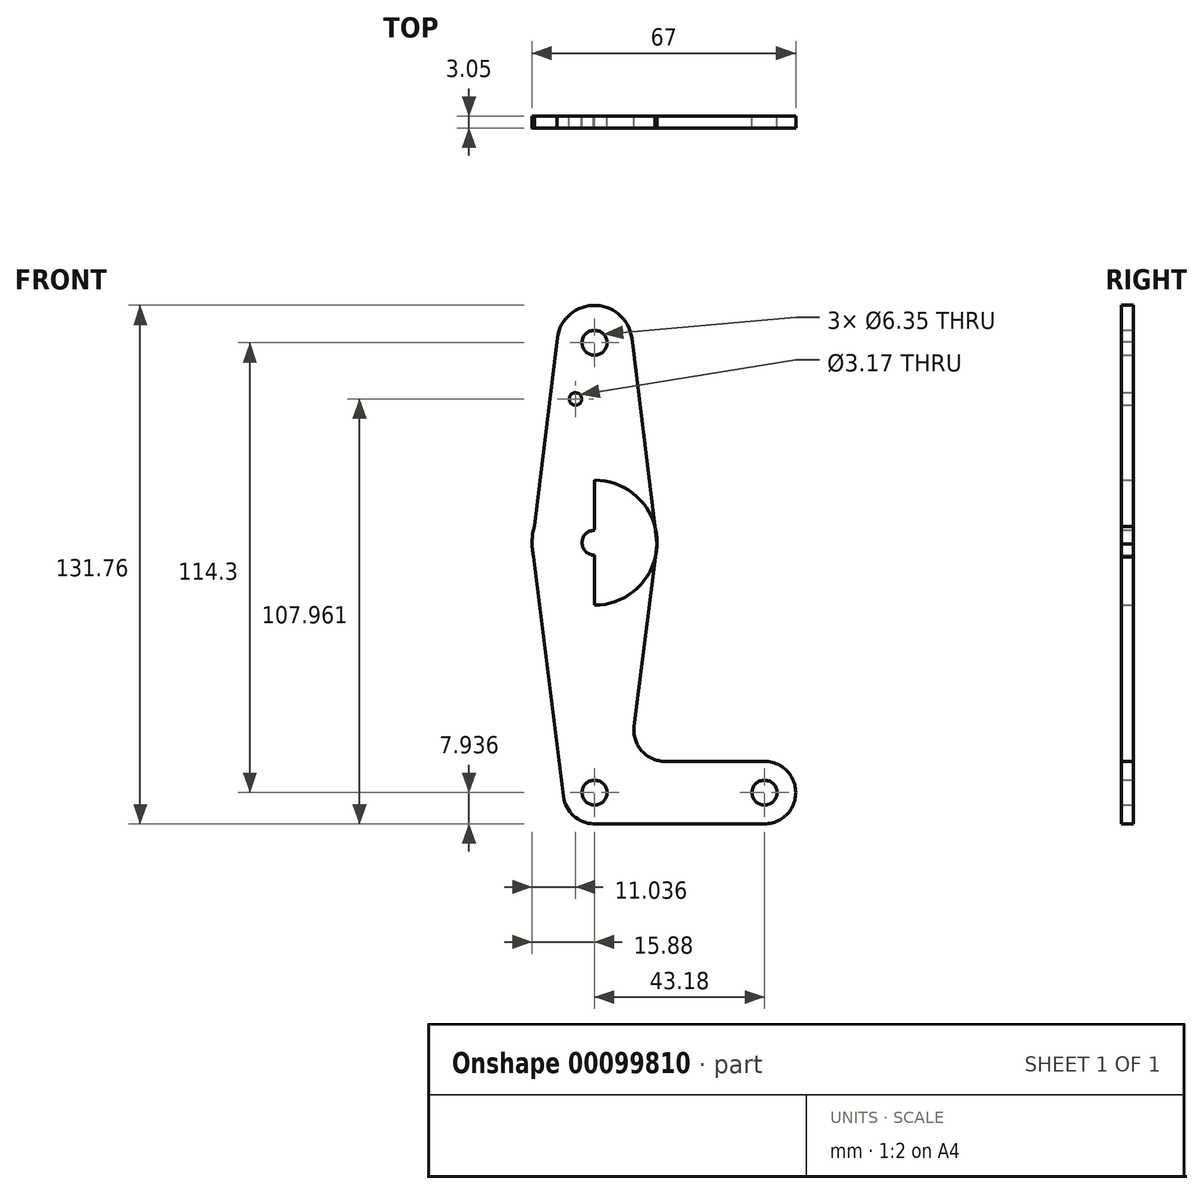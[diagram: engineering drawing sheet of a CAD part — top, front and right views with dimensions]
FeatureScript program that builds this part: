
annotation { "Feature Type Name" : "Feature", "Feature Type Description" : "" }
export const myFeature = defineFeature(function(context is Context, id is Id, definition is map)
    precondition{}
    {
        {
            var Q0;
            Q0=qCreatedBy(makeId("Front.planeOp"),FACE);
            var sketch = newSketch(context, id + "F0", { "sketchPlane" : qUnion([Q0])});
            skLineSegment(sketch, "E0", {"start": v(15.25, 82.35) * mm, "end": v(15.25, -31.95) * mm});
            skLineSegment(sketch, "E1", {"start": v(15.25, -31.95) * mm, "end": v(58.43, -31.95) * mm});
            skCircle(sketch, "E2", {"center": v(15.25, 82.35) * mm, "radius": 9.53 * mm});
            skCircle(sketch, "E3", {"center": v(15.25, 31.55) * mm, "radius": 15.88 * mm});
            skCircle(sketch, "E4", {"center": v(15.25, -31.95) * mm, "radius": 7.94 * mm});
            skCircle(sketch, "E5", {"center": v(58.43, -31.95) * mm, "radius": 7.94 * mm});
            skLineSegment(sketch, "E6", {"start": v(5.73, 82.64) * mm, "end": v(-0.62, 31.15) * mm});
            skLineSegment(sketch, "E7", {"start": v(-0.62, 31.15) * mm, "end": v(7.37, -32.94) * mm});
            skLineSegment(sketch, "E8", {"start": v(24.7, 83.5) * mm, "end": v(31.12, 31.25) * mm});
            skLineSegment(sketch, "E9", {"start": v(31.12, 31.25) * mm, "end": v(25.3, -15.08) * mm});
            skLineSegment(sketch, "E10", {"start": v(33.2, -24.02) * mm, "end": v(58.43, -24.02) * mm});
            skLineSegment(sketch, "E11", {"start": v(15.03, -39.89) * mm, "end": v(58.43, -39.9) * mm});
            skCircle(sketch, "E12", {"center": v(15.25, 82.35) * mm, "radius": 3.18 * mm});
            skCircle(sketch, "E13", {"center": v(15.25, 31.55) * mm, "radius": 3.18 * mm});
            skCircle(sketch, "E14", {"center": v(15.25, -31.95) * mm, "radius": 3.18 * mm});
            skCircle(sketch, "E15", {"center": v(58.43, -31.95) * mm, "radius": 3.18 * mm});
            skCircle(sketch, "E16", {"center": v(10.4, 68.07) * mm, "radius": 1.59 * mm});
            skArc(sketch, "E17.filletArc", {"start": v(25.3, -15.08) * mm, "mid": v(27.23, -21.33) * mm, "end": v(33.2, -24.02) * mm});
            skSolve(sketch);
        }
        {
            var Q0;
            {var subQ0=sQuery(id+"F0.wireOp",EDGE,"E4");var subQ1=sQuery(id+"F0.wireOp",EDGE,"E0");var subQ2=makeQuery(id+"F0.imprint","INTERSECT",VERTEX,{"derivedFrom":[subQ1,subQ0]});Q0=makeQuery(id+"F0.imprint","IMPRINT",FACE,{"disambiguationData":[TD([[makeQuery(id+"F0.imprint","IMPRINT",EDGE,{"disambiguationData":[TD([[subQ2,-1.0]])],"derivedFrom":subQ1}),1.0]])]});}
            var Q1;
            {var subQ0=sQuery(id+"F0.wireOp",EDGE,"E3");var subQ1=sQuery(id+"F0.wireOp",EDGE,"E0");var subQ2=makeQuery(id+"F0.imprint","INTERSECT",VERTEX,{"disambiguationData":[OD(1.0)],"derivedFrom":[subQ1,subQ0]});Q1=makeQuery(id+"F0.imprint","IMPRINT",FACE,{"disambiguationData":[TD([[makeQuery(id+"F0.imprint","IMPRINT",EDGE,{"disambiguationData":[TD([[subQ2,-1.0]])],"derivedFrom":subQ1}),-1.0]])]});}
            var Q2;
            {var subQ1=sQuery(id+"F0.wireOp",EDGE,"E3");var subQ3=sQuery(id+"F0.wireOp",EDGE,"E0");var subQ8=makeQuery(id+"F0.imprint","INTERSECT",VERTEX,{"disambiguationData":[OD(0.0)],"derivedFrom":[subQ3,subQ1]});Q2=makeQuery(id+"F0.imprint","IMPRINT",FACE,{"disambiguationData":[TD([[makeQuery(id+"F0.imprint","IMPRINT",EDGE,{"disambiguationData":[TD([[subQ8,-1.0]])],"derivedFrom":subQ3}),1.0]])]});}
            var Q3;
            {var subQ0=sQuery(id+"F0.wireOp",EDGE,"E5");var subQ1=sQuery(id+"F0.wireOp",EDGE,"E1");var subQ2=makeQuery(id+"F0.imprint","INTERSECT",VERTEX,{"derivedFrom":[subQ1,subQ0]});Q3=makeQuery(id+"F0.imprint","IMPRINT",FACE,{"disambiguationData":[TD([[makeQuery(id+"F0.imprint","IMPRINT",EDGE,{"disambiguationData":[TD([[subQ2,1.0]])],"derivedFrom":subQ1}),-1.0]])]});}
            var Q4;
            {var subQ11=sQuery(id+"F0.wireOp",EDGE,"E10");Q4=makeQuery(id+"F0.imprint","IMPRINT",FACE,{"disambiguationData":[TD([[makeQuery(id+"F0.imprint","IMPRINT",EDGE,{"derivedFrom":subQ11}),-1.0]])]});}
            var Q5;
            Q5=makeQuery(id+"F0.imprint","IMPRINT",FACE,{"disambiguationData":[TD([[makeQuery(id+"F0.imprint","IMPRINT",EDGE,{"derivedFrom":sQuery(id+"F0.wireOp",EDGE,"E12")}),-1.0]])]});
            var Q6;
            Q6=makeQuery(id+"F0.imprint","IMPRINT",FACE,{"disambiguationData":[TD([[makeQuery(id+"F0.imprint","IMPRINT",EDGE,{"derivedFrom":sQuery(id+"F0.wireOp",EDGE,"E16")}),-1.0]])]});
            var Q7;
            {var subQ0=sQuery(id+"F0.wireOp",EDGE,"E4");var subQ4=sQuery(id+"F0.wireOp",EDGE,"E0");var subQ5=makeQuery(id+"F0.imprint","INTERSECT",VERTEX,{"derivedFrom":[subQ4,subQ0]});Q7=makeQuery(id+"F0.imprint","IMPRINT",FACE,{"disambiguationData":[TD([[makeQuery(id+"F0.imprint","IMPRINT",EDGE,{"disambiguationData":[TD([[subQ5,-1.0]])],"derivedFrom":subQ4}),-1.0]])]});}
            var Q8;
            Q8=makeQuery(id+"F0.imprint","IMPRINT",FACE,{"disambiguationData":[TD([[makeQuery(id+"F0.imprint","IMPRINT",EDGE,{"derivedFrom":sQuery(id+"F0.wireOp",EDGE,"E15")}),-1.0]])]});
            var Q9;
            {var subQ1=sQuery(id+"F0.wireOp",EDGE,"E3");var subQ3=sQuery(id+"F0.wireOp",EDGE,"E0");var subQ7=makeQuery(id+"F0.imprint","INTERSECT",VERTEX,{"disambiguationData":[OD(0.0)],"derivedFrom":[subQ3,subQ1]});Q9=makeQuery(id+"F0.imprint","IMPRINT",FACE,{"disambiguationData":[TD([[makeQuery(id+"F0.imprint","IMPRINT",EDGE,{"disambiguationData":[TD([[subQ7,-1.0]])],"derivedFrom":subQ3}),-1.0]])]});}
            var Q10;
            {var subQ0=sQuery(id+"F0.wireOp",EDGE,"E2");var subQ1=sQuery(id+"F0.wireOp",EDGE,"E0");var subQ2=makeQuery(id+"F0.imprint","INTERSECT",VERTEX,{"derivedFrom":[subQ1,subQ0]});Q10=makeQuery(id+"F0.imprint","IMPRINT",FACE,{"disambiguationData":[TD([[makeQuery(id+"F0.imprint","IMPRINT",EDGE,{"disambiguationData":[TD([[subQ2,-1.0]])],"derivedFrom":subQ1}),1.0]])]});}
            var Q11;
            {var subQ0=sQuery(id+"F0.wireOp",EDGE,"E9");var subQ1=sQuery(id+"F0.wireOp",EDGE,"E3");var subQ3=makeQuery(id+"F0.imprint","INTERSECT",VERTEX,{"derivedFrom":[subQ1,subQ0]});Q11=makeQuery(id+"F0.imprint","IMPRINT",FACE,{"disambiguationData":[TD([[makeQuery(id+"F0.imprint","IMPRINT",EDGE,{"disambiguationData":[TD([[subQ3,-1.0]])],"derivedFrom":subQ1}),1.0]])]});}
            var Q12;
            {var subQ0=sQuery(id+"F0.wireOp",EDGE,"E7");var subQ1=sQuery(id+"F0.wireOp",EDGE,"E3");var subQ3=makeQuery(id+"F0.imprint","INTERSECT",VERTEX,{"derivedFrom":[subQ1,subQ0]});Q12=makeQuery(id+"F0.imprint","IMPRINT",FACE,{"disambiguationData":[TD([[makeQuery(id+"F0.imprint","IMPRINT",EDGE,{"disambiguationData":[TD([[subQ3,1.0]])],"derivedFrom":subQ1}),1.0]])]});}
            var Q13;
            {var subQ0=sQuery(id+"F0.wireOp",EDGE,"E6");var subQ1=sQuery(id+"F0.wireOp",EDGE,"E3");var subQ3=makeQuery(id+"F0.imprint","INTERSECT",VERTEX,{"derivedFrom":[subQ1,subQ0]});Q13=makeQuery(id+"F0.imprint","IMPRINT",FACE,{"disambiguationData":[TD([[makeQuery(id+"F0.imprint","IMPRINT",EDGE,{"disambiguationData":[TD([[subQ3,-1.0]])],"derivedFrom":subQ1}),1.0]])]});}
            var Q14;
            {var subQ0=sQuery(id+"F0.wireOp",EDGE,"E8");var subQ1=sQuery(id+"F0.wireOp",EDGE,"E3");var subQ3=makeQuery(id+"F0.imprint","INTERSECT",VERTEX,{"derivedFrom":[subQ1,subQ0]});Q14=makeQuery(id+"F0.imprint","IMPRINT",FACE,{"disambiguationData":[TD([[makeQuery(id+"F0.imprint","IMPRINT",EDGE,{"disambiguationData":[TD([[subQ3,1.0]])],"derivedFrom":subQ1}),1.0]])]});}
            var Q15;
            {var subQ0=sQuery(id+"F0.wireOp",EDGE,"E11");var subQ1=sQuery(id+"F0.wireOp",EDGE,"E4");var subQ2=makeQuery(id+"F0.imprint","INTERSECT",VERTEX,{"disambiguationData":[OD(0.0)],"derivedFrom":[subQ1,subQ0]});Q15=makeQuery(id+"F0.imprint","IMPRINT",FACE,{"disambiguationData":[TD([[makeQuery(id+"F0.imprint","IMPRINT",EDGE,{"disambiguationData":[TD([[subQ2,-1.0]])],"derivedFrom":subQ1}),1.0]])]});}
            extrude(context, id + "F1", {"entities" : qUnion([Q0, Q1, Q2, Q3, Q4, Q5, Q6, Q7, Q8, Q9, Q10, Q11, Q12, Q13, Q14, Q15]), "depth" : 3.05 * mm});
        }
    });
